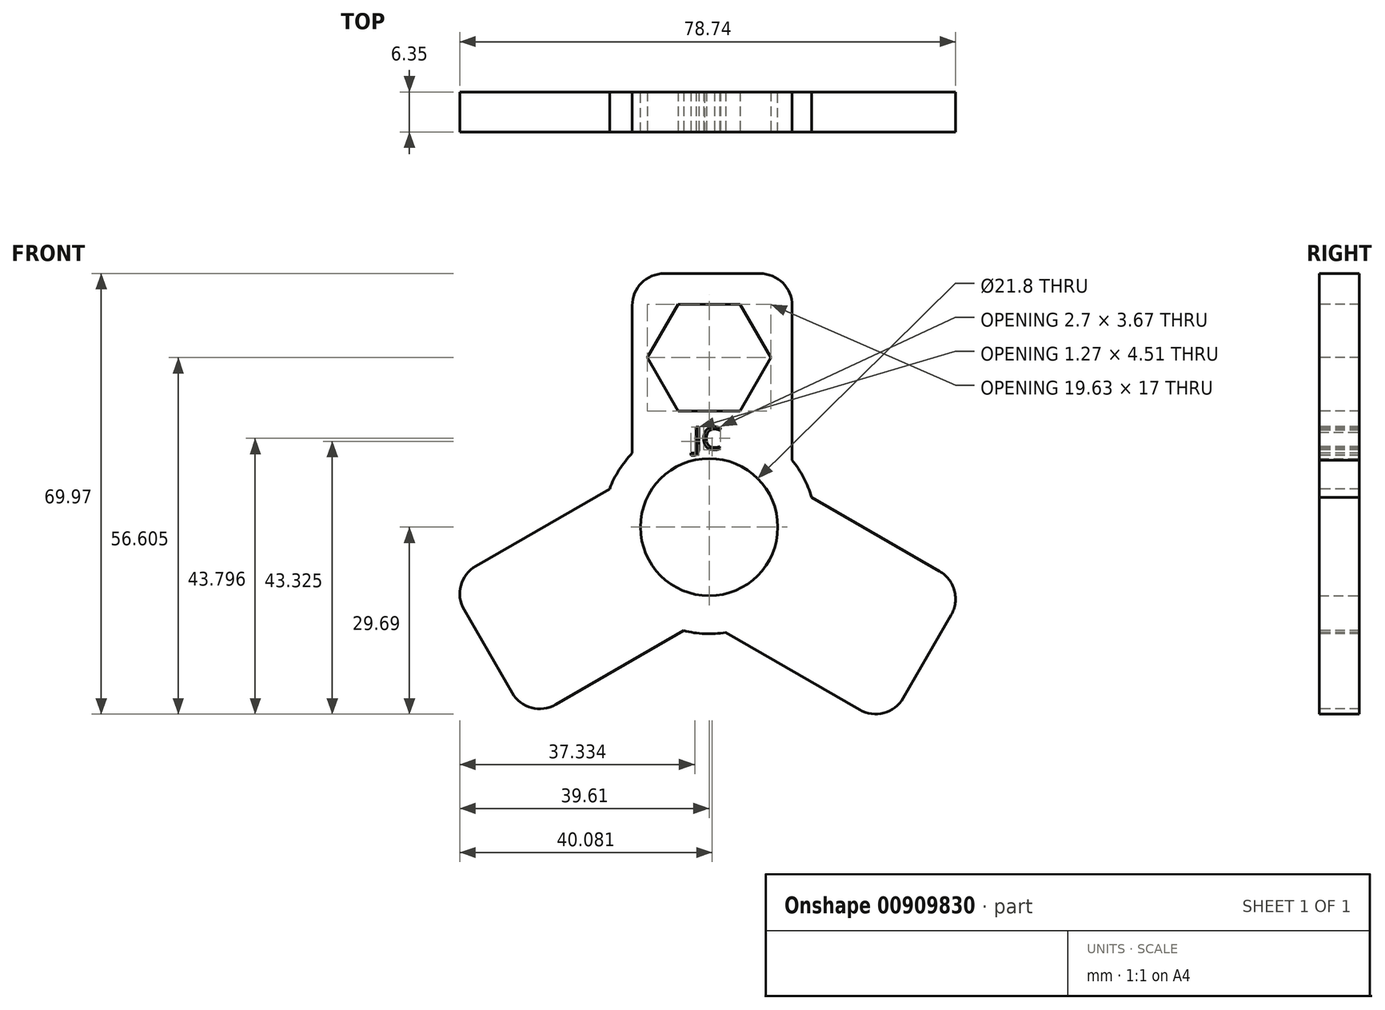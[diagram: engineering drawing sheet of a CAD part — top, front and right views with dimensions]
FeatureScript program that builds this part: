
annotation { "Feature Type Name" : "Feature", "Feature Type Description" : "" }
export const myFeature = defineFeature(function(context is Context, id is Id, definition is map)
    precondition{}
    {
        {
            var Q0;
            Q0=qCreatedBy(makeId("Front.planeOp"),FACE);
            var sketch = newSketch(context, id + "F0", { "sketchPlane" : qUnion([Q0])});
            skCircle(sketch, "E0", {"center": v(0, 0) * mm, "radius": 15.04 * mm});
            skLineSegment(sketch, "E1.bottom", {"start": v(13.18, 0) * mm, "end": v(-12.22, 0) * mm});
            skLineSegment(sketch, "E1.top", {"start": v(13.18, 40.28) * mm, "end": v(-12.22, 40.28) * mm});
            skLineSegment(sketch, "E1.left", {"start": v(13.18, 7.26) * mm, "end": v(13.18, 40.28) * mm});
            skLineSegment(sketch, "E1.right", {"start": v(-12.22, 8.77) * mm, "end": v(-12.22, 40.28) * mm});
            skLineSegment(sketch, "E2.1.0", {"start": v(-12.87, 7.78) * mm, "end": v(-41.47, -8.73) * mm});
            skLineSegment(sketch, "E2.1.1", {"start": v(-1.48, -14.97) * mm, "end": v(-28.77, -30.72) * mm});
            skLineSegment(sketch, "E2.1.2", {"start": v(-41.47, -8.73) * mm, "end": v(-28.77, -30.72) * mm});
            skLineSegment(sketch, "E2.2.0", {"start": v(-0.3, -15.04) * mm, "end": v(28.3, -31.55) * mm});
            skLineSegment(sketch, "E2.2.1", {"start": v(13.7, 6.2) * mm, "end": v(41, -9.55) * mm});
            skLineSegment(sketch, "E2.2.2", {"start": v(28.3, -31.55) * mm, "end": v(41, -9.55) * mm});
            skPoint(sketch, "E3.orphan", {"position": v(-6.59, 11.41) * mm});
            skPoint(sketch, "E4.orphan", {"position": v(6.11, 10.59) * mm});
            skPoint(sketch, "E5.orphan", {"position": v(-6.59, -11.41) * mm});
            skPoint(sketch, "E6.orphan", {"position": v(6.11, -10.59) * mm});
            skSolve(sketch);
        }
        {
            var Q0;
            Q0=makeQuery(id+"F0.imprint","IMPRINT",FACE,{"disambiguationData":[TD([[makeQuery(id+"F0.imprint","IMPRINT",EDGE,{"derivedFrom":sQuery(id+"F0.wireOp",EDGE,"E1.top")}),1.0]])]});
            var Q1;
            {var subQ0=sQuery(id+"F0.wireOp",EDGE,"E2.2.0");Q1=makeQuery(id+"F0.imprint","IMPRINT",FACE,{"disambiguationData":[TD([[makeQuery(id+"F0.imprint","IMPRINT",EDGE,{"derivedFrom":subQ0}),1.0]])]});}
            var Q2;
            {var subQ0=sQuery(id+"F0.wireOp",EDGE,"E0");var subQ4=makeQuery(id+"F0.imprint","INTERSECT",VERTEX,{"derivedFrom":[subQ0,sQuery(id+"F0.wireOp",EDGE,"E1.left")]});Q2=makeQuery(id+"F0.imprint","IMPRINT",FACE,{"disambiguationData":[TD([[makeQuery(id+"F0.imprint","IMPRINT",EDGE,{"disambiguationData":[TD([[subQ4,1.0]])],"derivedFrom":subQ0}),1.0]])]});}
            var Q3;
            {var subQ0=sQuery(id+"F0.wireOp",EDGE,"E2.1.0");Q3=makeQuery(id+"F0.imprint","IMPRINT",FACE,{"disambiguationData":[TD([[makeQuery(id+"F0.imprint","IMPRINT",EDGE,{"derivedFrom":subQ0}),1.0]])]});}
            extrude(context, id + "F1", {"entities" : qUnion([Q0, Q1, Q2, Q3]), "depth" : 6.35 * mm, "offsetDistance" : 25.4 * mm});
        }
        {
            var Q0;
            Q0=makeQuery(id+"F1.opExtrude","CAP_FACE",FACE,{"disambiguationData":[OSD([sQuery(id+"F0.wireOp",EDGE,"E0"),sQuery(id+"F0.wireOp",EDGE,"E1.top"),sQuery(id+"F0.wireOp",EDGE,"E1.left"),sQuery(id+"F0.wireOp",EDGE,"E1.right"),sQuery(id+"F0.wireOp",EDGE,"E2.1.0"),sQuery(id+"F0.wireOp",EDGE,"E2.1.1"),sQuery(id+"F0.wireOp",EDGE,"E2.1.2"),sQuery(id+"F0.wireOp",EDGE,"E2.2.0"),sQuery(id+"F0.wireOp",EDGE,"E2.2.1"),sQuery(id+"F0.wireOp",EDGE,"E2.2.2")])],"isStart":false});
            var sketch = newSketch(context, id + "F2", { "sketchPlane" : qUnion([Q0])});
            skCircle(sketch, "E7", {"center": v(0, 0) * mm, "radius": 16.95 * mm});
            skSolve(sketch);
        }
        {
            var Q0;
            Q0 = qSketchRegion(id + "F2", true);
            extrude(context, id + "F3", {"entities" : qUnion([Q0]), "operationType" : NewBodyOperationType.ADD, "oppositeDirection" : true, "depth" : 6.35 * mm, "offsetDistance" : 25.4 * mm});
        }
        {
            var Q0;
            Q0=makeQuery(id+"F3.boolean.opBoolean","MERGE",FACE,{"derivedFrom":[makeQuery(id+"F1.opExtrude","CAP_FACE",FACE,{"disambiguationData":[OSD([sQuery(id+"F0.wireOp",EDGE,"E0"),sQuery(id+"F0.wireOp",EDGE,"E1.top"),sQuery(id+"F0.wireOp",EDGE,"E1.left"),sQuery(id+"F0.wireOp",EDGE,"E1.right"),sQuery(id+"F0.wireOp",EDGE,"E2.1.0"),sQuery(id+"F0.wireOp",EDGE,"E2.1.1"),sQuery(id+"F0.wireOp",EDGE,"E2.1.2"),sQuery(id+"F0.wireOp",EDGE,"E2.2.0"),sQuery(id+"F0.wireOp",EDGE,"E2.2.1"),sQuery(id+"F0.wireOp",EDGE,"E2.2.2")])],"isStart":true}),makeQuery(id+"F3.opExtrude","CAP_FACE",FACE,{"disambiguationData":[OSD([sQuery(id+"F2.wireOp",EDGE,"E7")])],"isStart":false})]});
            var sketch = newSketch(context, id + "F4", { "sketchPlane" : qUnion([Q0])});
            skCircle(sketch, "E8", {"center": v(0, 0) * mm, "radius": 10.9 * mm});
            skSolve(sketch);
        }
        {
            var Q0;
            Q0 = qSketchRegion(id + "F4", true);
            extrude(context, id + "F5", {"entities" : qUnion([Q0]), "operationType" : NewBodyOperationType.REMOVE, "oppositeDirection" : true, "depth" : 25.4 * mm, "offsetDistance" : 25.4 * mm});
        }
        {
            var Q0;
            Q0=makeQuery(id+"F1.opExtrude","CAP_FACE",FACE,{"disambiguationData":[OSD([sQuery(id+"F0.wireOp",EDGE,"E0"),sQuery(id+"F0.wireOp",EDGE,"E1.top"),sQuery(id+"F0.wireOp",EDGE,"E1.left"),sQuery(id+"F0.wireOp",EDGE,"E1.right"),sQuery(id+"F0.wireOp",EDGE,"E2.1.0"),sQuery(id+"F0.wireOp",EDGE,"E2.1.1"),sQuery(id+"F0.wireOp",EDGE,"E2.1.2"),sQuery(id+"F0.wireOp",EDGE,"E2.2.0"),sQuery(id+"F0.wireOp",EDGE,"E2.2.1"),sQuery(id+"F0.wireOp",EDGE,"E2.2.2")])],"isStart":false});
            var sketch = newSketch(context, id + "F6", { "sketchPlane" : qUnion([Q0])});
            skText(sketch, "E9", { "text": "JC", "fontName": "OpenSans-Regular.ttf"});
            const initialGuessF6  = {"E9": [-0.00252, 0.01232, 1, 0, 0.0036]};
            skSetInitialGuess(sketch, initialGuessF6);
            skSolve(sketch);
        }
        {
            var Q0;
            Q0 = qSketchRegion(id + "F6", true);
            extrude(context, id + "F7", {"entities" : qUnion([Q0]), "operationType" : NewBodyOperationType.REMOVE, "oppositeDirection" : true, "depth" : 25.4 * mm, "offsetDistance" : 25.4 * mm});
        }
        {
            var Q0;
            Q0=makeQuery(id+"F3.boolean.opBoolean","MERGE",FACE,{"derivedFrom":[makeQuery(id+"F1.opExtrude","CAP_FACE",FACE,{"disambiguationData":[OSD([sQuery(id+"F0.wireOp",EDGE,"E0"),sQuery(id+"F0.wireOp",EDGE,"E1.top"),sQuery(id+"F0.wireOp",EDGE,"E1.left"),sQuery(id+"F0.wireOp",EDGE,"E1.right"),sQuery(id+"F0.wireOp",EDGE,"E2.1.0"),sQuery(id+"F0.wireOp",EDGE,"E2.1.1"),sQuery(id+"F0.wireOp",EDGE,"E2.1.2"),sQuery(id+"F0.wireOp",EDGE,"E2.2.0"),sQuery(id+"F0.wireOp",EDGE,"E2.2.1"),sQuery(id+"F0.wireOp",EDGE,"E2.2.2")])],"isStart":false}),makeQuery(id+"F3.opExtrude","CAP_FACE",FACE,{"disambiguationData":[OSD([sQuery(id+"F2.wireOp",EDGE,"E7")])],"isStart":true})]});
            var sketch = newSketch(context, id + "F8", { "sketchPlane" : qUnion([Q0])});
            skCircle(sketch, "E10.cCircle", {"center": v(0, 26.92) * mm, "radius": 8.5 * mm, "construction": true});
            skLineSegment(sketch, "E10.0", {"start": v(4.9, 18.42) * mm, "end": v(-4.9, 18.42) * mm});
            skLineSegment(sketch, "E10.1", {"start": v(-4.9, 18.42) * mm, "end": v(-9.81, 26.92) * mm});
            skLineSegment(sketch, "E10.2", {"start": v(-9.81, 26.92) * mm, "end": v(-4.9, 35.42) * mm});
            skLineSegment(sketch, "E10.3", {"start": v(-4.9, 35.42) * mm, "end": v(4.9, 35.42) * mm});
            skLineSegment(sketch, "E10.4", {"start": v(4.9, 35.42) * mm, "end": v(9.81, 26.92) * mm});
            skLineSegment(sketch, "E10.5", {"start": v(9.81, 26.92) * mm, "end": v(4.9, 18.42) * mm});
            skPoint(sketch, "E10.0.midPoint", {"position": v(0, 18.42) * mm});
            skSolve(sketch);
        }
        {
            var Q0;
            Q0=makeQuery(id+"F8.imprint","IMPRINT",FACE,{"disambiguationData":[TD([[makeQuery(id+"F8.imprint","IMPRINT",EDGE,{"derivedFrom":sQuery(id+"F8.wireOp",EDGE,"E10.0")}),-1.0]])]});
            extrude(context, id + "F9", {"entities" : qUnion([Q0]), "operationType" : NewBodyOperationType.REMOVE, "oppositeDirection" : true, "depth" : 25.4 * mm, "offsetDistance" : 25.4 * mm});
        }
        {
            var Q0;
            Q0=makeQuery(id+"F1.opExtrude","SWEPT_EDGE",EDGE,{"disambiguationData":[OSD([sQuery(id+"F0.wireOp",EDGE,"E1.top"),sQuery(id+"F0.wireOp",EDGE,"E1.right")])]});
            var Q1;
            Q1=makeQuery(id+"F1.opExtrude","SWEPT_EDGE",EDGE,{"disambiguationData":[OSD([sQuery(id+"F0.wireOp",EDGE,"E1.top"),sQuery(id+"F0.wireOp",EDGE,"E1.left")])]});
            var Q2;
            Q2=makeQuery(id+"F1.opExtrude","SWEPT_EDGE",EDGE,{"disambiguationData":[OSD([sQuery(id+"F0.wireOp",EDGE,"E2.1.0"),sQuery(id+"F0.wireOp",EDGE,"E2.1.2")])]});
            var Q3;
            Q3=makeQuery(id+"F1.opExtrude","SWEPT_EDGE",EDGE,{"disambiguationData":[OSD([sQuery(id+"F0.wireOp",EDGE,"E2.1.1"),sQuery(id+"F0.wireOp",EDGE,"E2.1.2")])]});
            var Q4;
            Q4=makeQuery(id+"F1.opExtrude","SWEPT_EDGE",EDGE,{"disambiguationData":[OSD([sQuery(id+"F0.wireOp",EDGE,"E2.2.0"),sQuery(id+"F0.wireOp",EDGE,"E2.2.2")])]});
            var Q5;
            Q5=makeQuery(id+"F1.opExtrude","SWEPT_EDGE",EDGE,{"disambiguationData":[OSD([sQuery(id+"F0.wireOp",EDGE,"E2.2.1"),sQuery(id+"F0.wireOp",EDGE,"E2.2.2")])]});
            fillet(context, id + "F10", {"entities" : qUnion([Q0, Q1, Q2, Q3, Q4, Q5]), "radius" : 5.08 * mm, "tangentPropagation" : true, "allowEdgeOverflow" : false});
        }
    });
